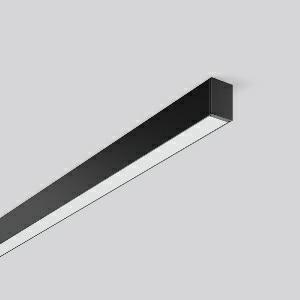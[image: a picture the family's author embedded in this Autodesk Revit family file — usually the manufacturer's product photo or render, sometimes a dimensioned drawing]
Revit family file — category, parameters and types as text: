
# Revit family: less_is_more_27_312198_003_8b3a
name_source: partatom
category: Lighting Fixtures
units: mm (PartAtom-declared; Revit-internal decimal feet)

## family parameters
Cut with Voids When Loaded = No
Host = Face
Light Source = No
Part Type = Normal
Room Calculation Point = No
Round Connector Dimension = Use Diameter
Shared = No

## types (1)
- LESS IS MORE 27 (1 x LED Modul 830, 1900 lm, 3000)
    Apparent Load = 35 VA
    CIE Flux Codes = 48 79 96 100 100
    Color Rendering = 80
    Color Temperature = 3000
    Default Elevation = 1800 mm
    Description = Series: LESS IS MORE 27
Ceiling and wall luminaire with slim design. Housing: extruded aluminium profile, powder-coated. End cap aluminium powder-coated. Diffuser made of non-yellowing plastic (PMMA), opal. Suitable for Ceiling mounting, Wall (surface). External driver with connecting cable. 
Colour: deep black, matt (RAL 9005)
Length: 1212 mm
Width: 28 mm
Height: 38 mm
Lamp: LED
Socket: without socket
Colour temperature: 3000K
Colour rendering index (CRI): 82
System power: 35 W
Rated luminous flux: 1900 lm
Beam angle Down: 110° / 109°
Luminous efficiency: 54 lm/W
Control gear: Regulated power supply
Protection class: II
Type of protection: IP 20
    Height = 38 mm
    Lamp = 1 x LED Modul 830
    Lamp Light Flux = 1900 lm
    Lamp count = 1
    Length = 1212 mm
    Lifetime = 50000 h
    Luminous efficacy = 54 lm/W
    Manufacturer = RZB
    ModVariant = No
    Model = 312198.003
    Mounting Place = Ceiling, Wall
    Mounting Type = Surface mounted
    Number of Poles = 1
    OnlyDefault = Yes
    Power Factor = 1
    Product Name = LESS IS MORE 27
    Product group = Surface mounted LED linear luminaires
    ProductGroupID = 307
    Protection Class = Protection class II
    Protection Degree = IP 20
    RLX_Detail_Level = 1
    RLX_Emergency_Light_Flux = 0 lm
    RLX_Emergency_Type = 0
    RLX_Emergency_Type_DB = No
    RlxData = <blob elided: 28705 chars, md5=7835bd84>
    Socket = socket
    Standby Power = 0 W
    System Light Flux = 1900 lm
    System Power = 35 W
    Type Comments = ALEA SPOT
    Type Image = 312196.003.jpg
    URL = http://relux.com
    VarID = ---
    Voltage = 230 V
    Voltage Range = 220-240 V
    Weight = 0.00 kg
    Width = 28 mm

## geometry (parser evidence)
native form markers: Blend x4, Sweep x12
no freeform markers — native parametric forms only
